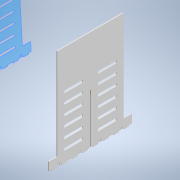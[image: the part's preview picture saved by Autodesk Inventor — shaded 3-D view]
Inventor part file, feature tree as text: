
AUTODESK INVENTOR PART (.ipt)
format: ipt  version: 2021.1 (Build 251245010, 245A)  size: 393,216 bytes
history: native  units: mm
features: reference x17, other x5, extrude x3, sketch x3
ambient origin geometry x8: Origin, YZ Plane, XZ Plane, XY Plane, X Axis, Y Axis, Z Axis, Center Point
bodies: Body1 (feature_tree)
feature tree (28):
  other  "Твердое тело1"
  other  "РабПлоскость1"
  extrude  "Корпус"  Depth=400.0mm
  extrude  "Отверстия"  Depth=500.0mm
  extrude  "Пазы"  Depth=6.2mm
  sketch  "Эскиз1"
  reference  "Ссылка1"
  reference  "Ссылка2"
  reference  "Ссылка3"
  reference  "Ссылка4"
  reference  "Ссылка5"
  reference  "Ссылка6"
  reference  "Ссылка7"
  reference  "Ссылка8"
  reference  "Ссылка9"
  reference  "Ссылка10"
  reference  "Ссылка11"
  reference  "Ссылка12"
  reference  "Ссылка13"
  reference  "Ссылка14"
  reference  "Ссылка15"
  reference  "Ссылка16"
  reference  "Ссылка17"
  sketch  "Эскиз2"
  sketch  "Эскиз3"
  other  "<userpath>\Documents\Savka\3d\Korp.iam"
  other  "Korp.iam"
  other  "Korpus:1"
